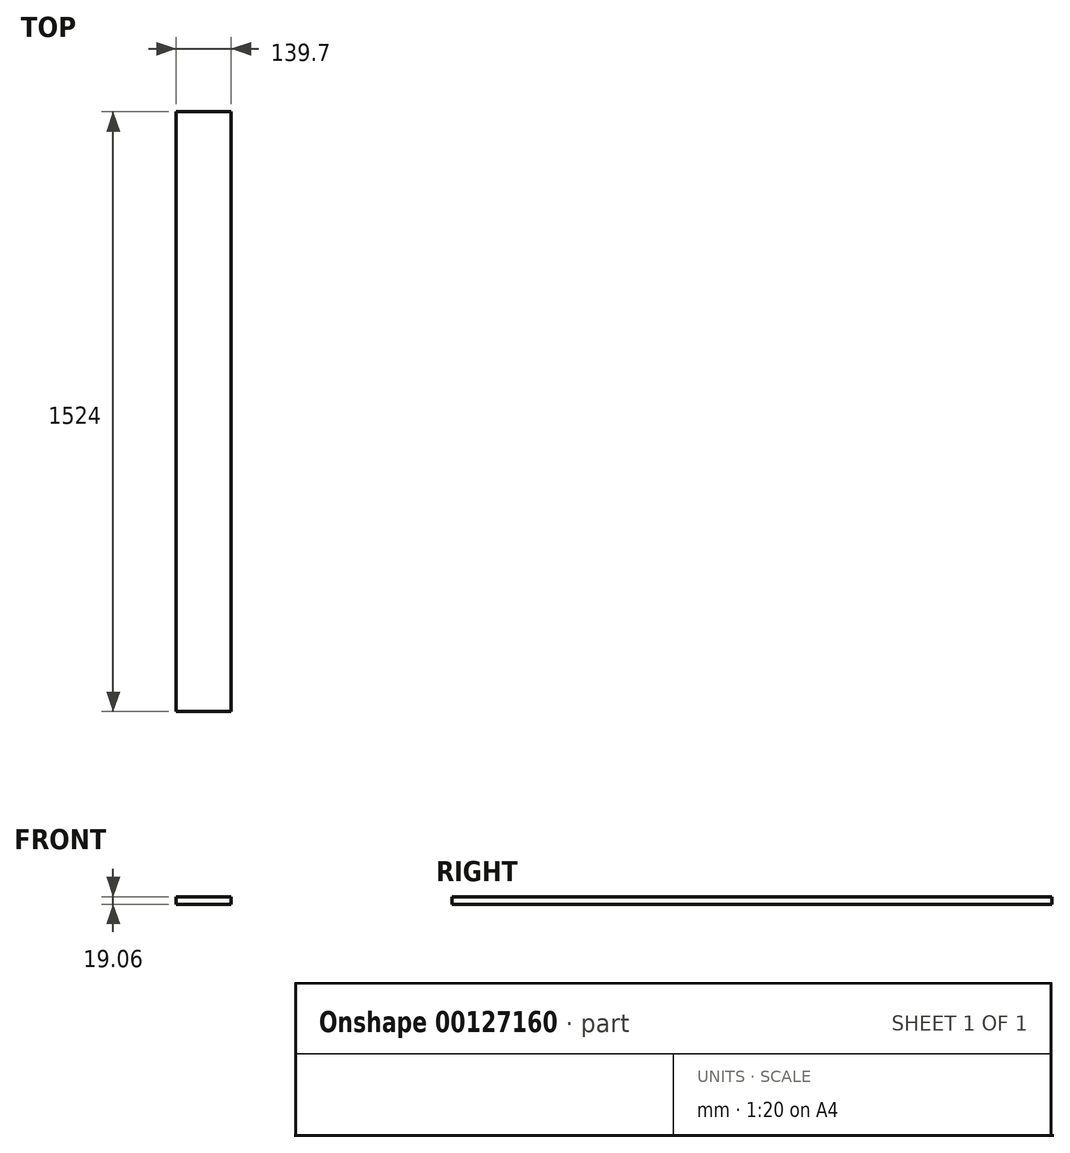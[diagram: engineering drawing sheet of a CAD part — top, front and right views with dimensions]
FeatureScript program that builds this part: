
annotation { "Feature Type Name" : "Feature", "Feature Type Description" : "" }
export const myFeature = defineFeature(function(context is Context, id is Id, definition is map)
    precondition{}
    {
        {
            var Q0;
            Q0=qCreatedBy(makeId("Front.planeOp"),FACE);
            var sketch = newSketch(context, id + "F0", { "sketchPlane" : qUnion([Q0])});
            skLineSegment(sketch, "E0.bottom", {"start": v(69.85, -9.52) * mm, "end": v(-69.85, -9.53) * mm});
            skLineSegment(sketch, "E0.top", {"start": v(69.85, 9.53) * mm, "end": v(-69.85, 9.52) * mm});
            skLineSegment(sketch, "E0.left", {"start": v(69.85, -9.53) * mm, "end": v(69.85, 9.53) * mm});
            skLineSegment(sketch, "E0.right", {"start": v(-69.85, -9.53) * mm, "end": v(-69.85, 9.52) * mm});
            skPoint(sketch, "E0.middle", {"position": v(0, 0) * mm});
            skSolve(sketch);
        }
        {
            var Q0;
            Q0=qSketchRegion(id+"F0",true);
            extrude(context, id + "F1", {"entities" : qUnion([Q0]), "depth" : 1524 * mm});
        }
    });
